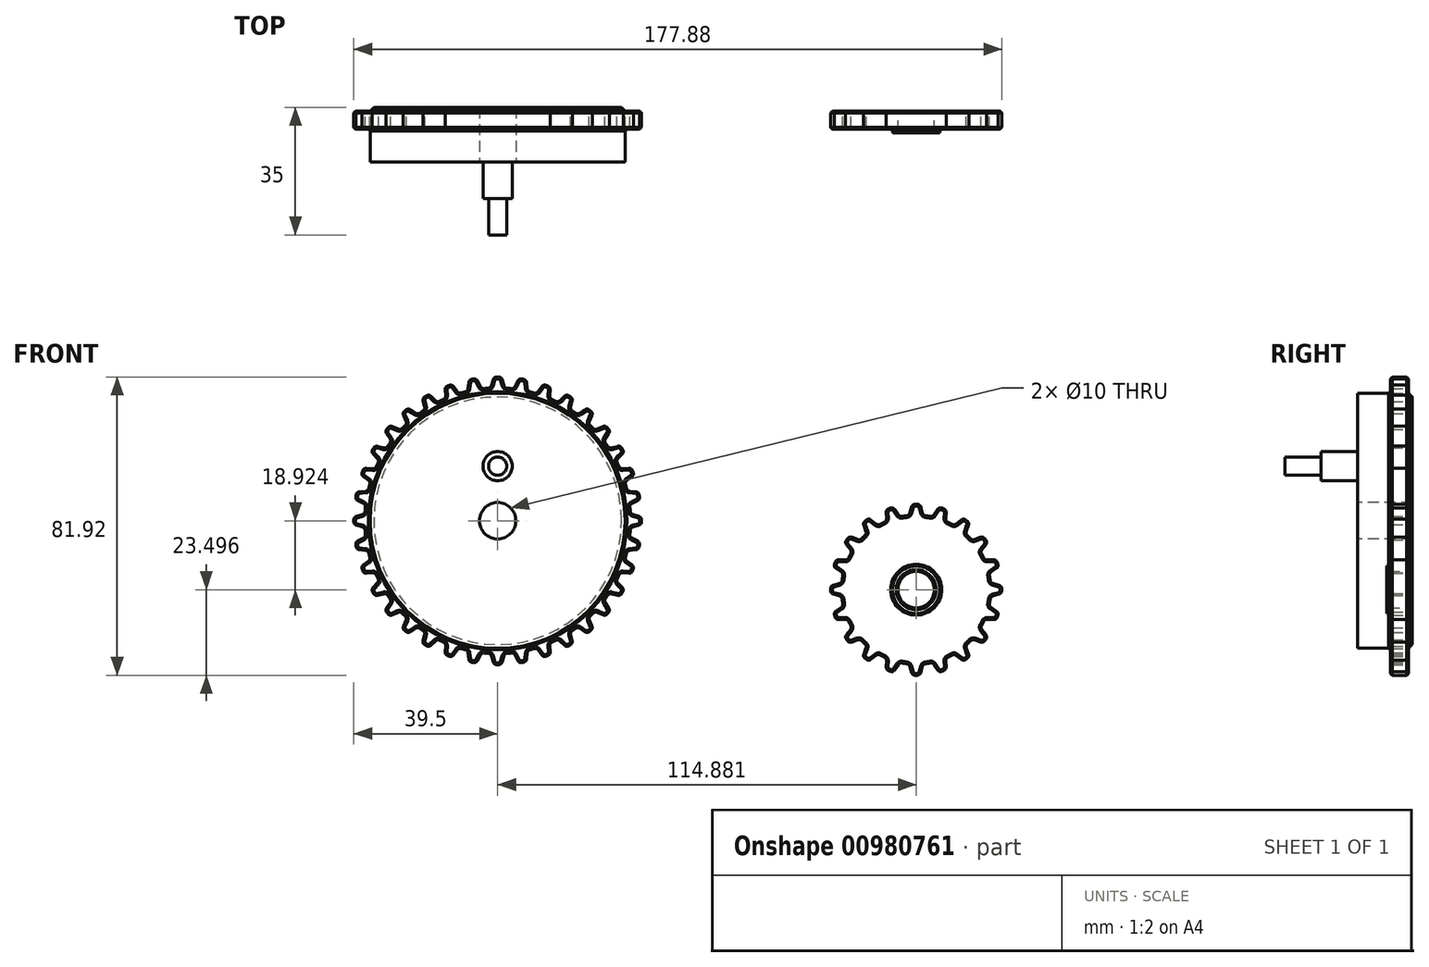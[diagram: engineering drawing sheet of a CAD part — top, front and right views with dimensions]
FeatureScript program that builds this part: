
annotation { "Feature Type Name" : "Feature", "Feature Type Description" : "" }
export const myFeature = defineFeature(function(context is Context, id is Id, definition is map)
    precondition{}
    {
        {
            var Q0;
            Q0=qCreatedBy(makeId("Front.planeOp"),FACE);
            var sketch = newSketch(context, id + "F0", { "sketchPlane" : qUnion([Q0])});
            skArc(sketch, "E0", {"start": v(1.03, 39.49) * mm, "mid": v(0, 39.5) * mm, "end": v(-1.03, 39.49) * mm});
            skCircle(sketch, "E1", {"center": v(0, 0) * mm, "radius": 36.5 * mm});
            skLineSegment(sketch, "E2", {"start": v(0, 0) * mm, "end": v(0, 36.5) * mm});
            skLineSegment(sketch, "E3", {"start": v(-1.03, 39.49) * mm, "end": v(-1.91, 36.45) * mm});
            skLineSegment(sketch, "E4", {"start": v(1.03, 39.49) * mm, "end": v(1.91, 36.45) * mm});
            skSolve(sketch);
        }
        {
            var Q0;
            {var subQ0=sQuery(id+"F0.wireOp",EDGE,"E1");var subQ1=makeQuery(id+"F0.imprint","IMPRINT",VERTEX,{"derivedFrom":subQ0});Q0=makeQuery(id+"F0.imprint","IMPRINT",FACE,{"disambiguationData":[TD([[makeQuery(id+"F0.imprint","IMPRINT",EDGE,{"disambiguationData":[TD([[subQ1,1.0]])],"derivedFrom":subQ0}),1.0]])]});}
            var Q1;
            Q1=makeQuery(id+"F0.imprint","IMPRINT",FACE,{"disambiguationData":[TD([[makeQuery(id+"F0.imprint","IMPRINT",EDGE,{"derivedFrom":sQuery(id+"F0.wireOp",EDGE,"E0")}),1.0]])]});
            extrude(context, id + "F1", {"entities" : qUnion([Q0, Q1]), "depth" : 5 * mm, "offsetDistance" : 25 * mm, "symmetric" : true});
        }
        {
            var Q0;
            Q0=makeQuery(id+"F1.opExtrude","SWEPT_EDGE",EDGE,{"disambiguationData":[OSD([sQuery(id+"F0.wireOp",EDGE,"E0"),sQuery(id+"F0.wireOp",EDGE,"E3")])]});
            var Q1;
            Q1=makeQuery(id+"F1.opExtrude","SWEPT_EDGE",EDGE,{"disambiguationData":[OSD([sQuery(id+"F0.wireOp",EDGE,"E0"),sQuery(id+"F0.wireOp",EDGE,"E4")])]});
            var Q2;
            Q2=makeQuery(id+"F1.opExtrude","SWEPT_EDGE",EDGE,{"disambiguationData":[OSD([sQuery(id+"F0.wireOp",EDGE,"E1"),sQuery(id+"F0.wireOp",EDGE,"E3")])]});
            var Q3;
            Q3=makeQuery(id+"F1.opExtrude","SWEPT_EDGE",EDGE,{"disambiguationData":[OSD([sQuery(id+"F0.wireOp",EDGE,"E1"),sQuery(id+"F0.wireOp",EDGE,"E4")])]});
            fillet(context, id + "F2", {"entities" : qUnion([Q0, Q1, Q2, Q3]), "radius" : 1 * mm, "tangentPropagation" : true, "allowEdgeOverflow" : false});
        }
        {
            var Q0;
            Q0=makeQuery(id+"F1.opExtrude","SWEPT_BODY",BODY,{"disambiguationData":[OSD([sQuery(id+"F0.wireOp",EDGE,"E0"),sQuery(id+"F0.wireOp",EDGE,"E1"),sQuery(id+"F0.wireOp",EDGE,"E3"),sQuery(id+"F0.wireOp",EDGE,"E4")])]});
            var Q1;
            Q1=makeQuery(id+"F1.opExtrude","SWEPT_FACE",FACE,{"disambiguationData":[OSD([sQuery(id+"F0.wireOp",EDGE,"E1")])]});
            circularPattern(context, id + "F3", {"operationType" : NewBodyOperationType.ADD, "entities" : qUnion([Q0]), "axis" : qUnion([Q1]), "angle" : 360 * degree, "instanceCount" : 36, "equalSpace" : true});
        }
        {
            var Q0;
            {var subQ0=makeQuery(id+"F1.opExtrude","CAP_FACE",FACE,{"disambiguationData":[OSD([sQuery(id+"F0.wireOp",EDGE,"E0"),sQuery(id+"F0.wireOp",EDGE,"E1"),sQuery(id+"F0.wireOp",EDGE,"E3"),sQuery(id+"F0.wireOp",EDGE,"E4")])],"isStart":false});Q0=makeQuery(id+"F3.boolean.opBoolean","MERGE",FACE,{"derivedFrom":[subQ0,makeQuery(id+"F3.opPattern","COPY",FACE,{"derivedFrom":subQ0,"instanceName":"1"}),makeQuery(id+"F3.opPattern","COPY",FACE,{"derivedFrom":subQ0,"instanceName":"2"}),makeQuery(id+"F3.opPattern","COPY",FACE,{"derivedFrom":subQ0,"instanceName":"3"}),makeQuery(id+"F3.opPattern","COPY",FACE,{"derivedFrom":subQ0,"instanceName":"4"}),makeQuery(id+"F3.opPattern","COPY",FACE,{"derivedFrom":subQ0,"instanceName":"5"}),makeQuery(id+"F3.opPattern","COPY",FACE,{"derivedFrom":subQ0,"instanceName":"6"}),makeQuery(id+"F3.opPattern","COPY",FACE,{"derivedFrom":subQ0,"instanceName":"7"}),makeQuery(id+"F3.opPattern","COPY",FACE,{"derivedFrom":subQ0,"instanceName":"8"}),makeQuery(id+"F3.opPattern","COPY",FACE,{"derivedFrom":subQ0,"instanceName":"9"}),makeQuery(id+"F3.opPattern","COPY",FACE,{"derivedFrom":subQ0,"instanceName":"10"}),makeQuery(id+"F3.opPattern","COPY",FACE,{"derivedFrom":subQ0,"instanceName":"11"}),makeQuery(id+"F3.opPattern","COPY",FACE,{"derivedFrom":subQ0,"instanceName":"12"}),makeQuery(id+"F3.opPattern","COPY",FACE,{"derivedFrom":subQ0,"instanceName":"13"}),makeQuery(id+"F3.opPattern","COPY",FACE,{"derivedFrom":subQ0,"instanceName":"14"}),makeQuery(id+"F3.opPattern","COPY",FACE,{"derivedFrom":subQ0,"instanceName":"15"}),makeQuery(id+"F3.opPattern","COPY",FACE,{"derivedFrom":subQ0,"instanceName":"16"}),makeQuery(id+"F3.opPattern","COPY",FACE,{"derivedFrom":subQ0,"instanceName":"17"}),makeQuery(id+"F3.opPattern","COPY",FACE,{"derivedFrom":subQ0,"instanceName":"18"}),makeQuery(id+"F3.opPattern","COPY",FACE,{"derivedFrom":subQ0,"instanceName":"19"}),makeQuery(id+"F3.opPattern","COPY",FACE,{"derivedFrom":subQ0,"instanceName":"20"}),makeQuery(id+"F3.opPattern","COPY",FACE,{"derivedFrom":subQ0,"instanceName":"21"}),makeQuery(id+"F3.opPattern","COPY",FACE,{"derivedFrom":subQ0,"instanceName":"22"}),makeQuery(id+"F3.opPattern","COPY",FACE,{"derivedFrom":subQ0,"instanceName":"23"}),makeQuery(id+"F3.opPattern","COPY",FACE,{"derivedFrom":subQ0,"instanceName":"24"}),makeQuery(id+"F3.opPattern","COPY",FACE,{"derivedFrom":subQ0,"instanceName":"25"}),makeQuery(id+"F3.opPattern","COPY",FACE,{"derivedFrom":subQ0,"instanceName":"26"}),makeQuery(id+"F3.opPattern","COPY",FACE,{"derivedFrom":subQ0,"instanceName":"27"}),makeQuery(id+"F3.opPattern","COPY",FACE,{"derivedFrom":subQ0,"instanceName":"28"}),makeQuery(id+"F3.opPattern","COPY",FACE,{"derivedFrom":subQ0,"instanceName":"29"}),makeQuery(id+"F3.opPattern","COPY",FACE,{"derivedFrom":subQ0,"instanceName":"30"}),makeQuery(id+"F3.opPattern","COPY",FACE,{"derivedFrom":subQ0,"instanceName":"31"}),makeQuery(id+"F3.opPattern","COPY",FACE,{"derivedFrom":subQ0,"instanceName":"32"}),makeQuery(id+"F3.opPattern","COPY",FACE,{"derivedFrom":subQ0,"instanceName":"33"}),makeQuery(id+"F3.opPattern","COPY",FACE,{"derivedFrom":subQ0,"instanceName":"34"}),makeQuery(id+"F3.opPattern","COPY",FACE,{"derivedFrom":subQ0,"instanceName":"35"})]});}
            var sketch = newSketch(context, id + "F4", { "sketchPlane" : qUnion([Q0])});
            skCircle(sketch, "E5", {"center": v(0, 0) * mm, "radius": 35 * mm});
            skSolve(sketch);
        }
        {
            var Q0;
            Q0=makeQuery(id+"F4.imprint","IMPRINT",FACE,{"disambiguationData":[TD([[makeQuery(id+"F4.imprint","IMPRINT",EDGE,{"derivedFrom":sQuery(id+"F4.wireOp",EDGE,"E5")}),1.0]])]});
            extrude(context, id + "F5", {"entities" : qUnion([Q0]), "operationType" : NewBodyOperationType.ADD, "depth" : 9 * mm, "offsetDistance" : 25 * mm});
        }
        {
            var Q0;
            {var subQ0=makeQuery(id+"F1.opExtrude","CAP_FACE",FACE,{"disambiguationData":[OSD([sQuery(id+"F0.wireOp",EDGE,"E0"),sQuery(id+"F0.wireOp",EDGE,"E1"),sQuery(id+"F0.wireOp",EDGE,"E3"),sQuery(id+"F0.wireOp",EDGE,"E4")])],"isStart":true});Q0=makeQuery(id+"F3.boolean.opBoolean","MERGE",FACE,{"derivedFrom":[subQ0,makeQuery(id+"F3.opPattern","COPY",FACE,{"derivedFrom":subQ0,"instanceName":"1"}),makeQuery(id+"F3.opPattern","COPY",FACE,{"derivedFrom":subQ0,"instanceName":"2"}),makeQuery(id+"F3.opPattern","COPY",FACE,{"derivedFrom":subQ0,"instanceName":"3"}),makeQuery(id+"F3.opPattern","COPY",FACE,{"derivedFrom":subQ0,"instanceName":"4"}),makeQuery(id+"F3.opPattern","COPY",FACE,{"derivedFrom":subQ0,"instanceName":"5"}),makeQuery(id+"F3.opPattern","COPY",FACE,{"derivedFrom":subQ0,"instanceName":"6"}),makeQuery(id+"F3.opPattern","COPY",FACE,{"derivedFrom":subQ0,"instanceName":"7"}),makeQuery(id+"F3.opPattern","COPY",FACE,{"derivedFrom":subQ0,"instanceName":"8"}),makeQuery(id+"F3.opPattern","COPY",FACE,{"derivedFrom":subQ0,"instanceName":"9"}),makeQuery(id+"F3.opPattern","COPY",FACE,{"derivedFrom":subQ0,"instanceName":"10"}),makeQuery(id+"F3.opPattern","COPY",FACE,{"derivedFrom":subQ0,"instanceName":"11"}),makeQuery(id+"F3.opPattern","COPY",FACE,{"derivedFrom":subQ0,"instanceName":"12"}),makeQuery(id+"F3.opPattern","COPY",FACE,{"derivedFrom":subQ0,"instanceName":"13"}),makeQuery(id+"F3.opPattern","COPY",FACE,{"derivedFrom":subQ0,"instanceName":"14"}),makeQuery(id+"F3.opPattern","COPY",FACE,{"derivedFrom":subQ0,"instanceName":"15"}),makeQuery(id+"F3.opPattern","COPY",FACE,{"derivedFrom":subQ0,"instanceName":"16"}),makeQuery(id+"F3.opPattern","COPY",FACE,{"derivedFrom":subQ0,"instanceName":"17"}),makeQuery(id+"F3.opPattern","COPY",FACE,{"derivedFrom":subQ0,"instanceName":"18"}),makeQuery(id+"F3.opPattern","COPY",FACE,{"derivedFrom":subQ0,"instanceName":"19"}),makeQuery(id+"F3.opPattern","COPY",FACE,{"derivedFrom":subQ0,"instanceName":"20"}),makeQuery(id+"F3.opPattern","COPY",FACE,{"derivedFrom":subQ0,"instanceName":"21"}),makeQuery(id+"F3.opPattern","COPY",FACE,{"derivedFrom":subQ0,"instanceName":"22"}),makeQuery(id+"F3.opPattern","COPY",FACE,{"derivedFrom":subQ0,"instanceName":"23"}),makeQuery(id+"F3.opPattern","COPY",FACE,{"derivedFrom":subQ0,"instanceName":"24"}),makeQuery(id+"F3.opPattern","COPY",FACE,{"derivedFrom":subQ0,"instanceName":"25"}),makeQuery(id+"F3.opPattern","COPY",FACE,{"derivedFrom":subQ0,"instanceName":"26"}),makeQuery(id+"F3.opPattern","COPY",FACE,{"derivedFrom":subQ0,"instanceName":"27"}),makeQuery(id+"F3.opPattern","COPY",FACE,{"derivedFrom":subQ0,"instanceName":"28"}),makeQuery(id+"F3.opPattern","COPY",FACE,{"derivedFrom":subQ0,"instanceName":"29"}),makeQuery(id+"F3.opPattern","COPY",FACE,{"derivedFrom":subQ0,"instanceName":"30"}),makeQuery(id+"F3.opPattern","COPY",FACE,{"derivedFrom":subQ0,"instanceName":"31"}),makeQuery(id+"F3.opPattern","COPY",FACE,{"derivedFrom":subQ0,"instanceName":"32"}),makeQuery(id+"F3.opPattern","COPY",FACE,{"derivedFrom":subQ0,"instanceName":"33"}),makeQuery(id+"F3.opPattern","COPY",FACE,{"derivedFrom":subQ0,"instanceName":"34"}),makeQuery(id+"F3.opPattern","COPY",FACE,{"derivedFrom":subQ0,"instanceName":"35"})]});}
            var sketch = newSketch(context, id + "F6", { "sketchPlane" : qUnion([Q0])});
            skCircle(sketch, "E6", {"center": v(0, 0) * mm, "radius": 35 * mm});
            skSolve(sketch);
        }
        {
            var Q0;
            Q0 = qSketchRegion(id + "F6", true);
            extrude(context, id + "F7", {"entities" : qUnion([Q0]), "operationType" : NewBodyOperationType.ADD, "depth" : 1 * mm, "offsetDistance" : 25 * mm});
        }
        {
            var Q0;
            Q0=makeQuery(id+"F7.opExtrude","CAP_EDGE",EDGE,{"disambiguationData":[OSD([sQuery(id+"F6.wireOp",EDGE,"E6")])],"isStart":false});
            chamfer(context, id + "F8", {"entities" : qUnion([Q0]), "width" : 1 * mm, "tangentPropagation" : true});
        }
        {
            var Q0;
            {var subQ0=makeQuery(id+"F1.opExtrude","CAP_FACE",FACE,{"disambiguationData":[OSD([sQuery(id+"F0.wireOp",EDGE,"E0"),sQuery(id+"F0.wireOp",EDGE,"E1"),sQuery(id+"F0.wireOp",EDGE,"E3"),sQuery(id+"F0.wireOp",EDGE,"E4")])],"isStart":false});Q0=makeQuery(id+"F3.boolean.opBoolean","MERGE",FACE,{"derivedFrom":[subQ0,makeQuery(id+"F3.opPattern","COPY",FACE,{"derivedFrom":subQ0,"instanceName":"1"}),makeQuery(id+"F3.opPattern","COPY",FACE,{"derivedFrom":subQ0,"instanceName":"2"}),makeQuery(id+"F3.opPattern","COPY",FACE,{"derivedFrom":subQ0,"instanceName":"3"}),makeQuery(id+"F3.opPattern","COPY",FACE,{"derivedFrom":subQ0,"instanceName":"4"}),makeQuery(id+"F3.opPattern","COPY",FACE,{"derivedFrom":subQ0,"instanceName":"5"}),makeQuery(id+"F3.opPattern","COPY",FACE,{"derivedFrom":subQ0,"instanceName":"6"}),makeQuery(id+"F3.opPattern","COPY",FACE,{"derivedFrom":subQ0,"instanceName":"7"}),makeQuery(id+"F3.opPattern","COPY",FACE,{"derivedFrom":subQ0,"instanceName":"8"}),makeQuery(id+"F3.opPattern","COPY",FACE,{"derivedFrom":subQ0,"instanceName":"9"}),makeQuery(id+"F3.opPattern","COPY",FACE,{"derivedFrom":subQ0,"instanceName":"10"}),makeQuery(id+"F3.opPattern","COPY",FACE,{"derivedFrom":subQ0,"instanceName":"11"}),makeQuery(id+"F3.opPattern","COPY",FACE,{"derivedFrom":subQ0,"instanceName":"12"}),makeQuery(id+"F3.opPattern","COPY",FACE,{"derivedFrom":subQ0,"instanceName":"13"}),makeQuery(id+"F3.opPattern","COPY",FACE,{"derivedFrom":subQ0,"instanceName":"14"}),makeQuery(id+"F3.opPattern","COPY",FACE,{"derivedFrom":subQ0,"instanceName":"15"}),makeQuery(id+"F3.opPattern","COPY",FACE,{"derivedFrom":subQ0,"instanceName":"16"}),makeQuery(id+"F3.opPattern","COPY",FACE,{"derivedFrom":subQ0,"instanceName":"17"}),makeQuery(id+"F3.opPattern","COPY",FACE,{"derivedFrom":subQ0,"instanceName":"18"}),makeQuery(id+"F3.opPattern","COPY",FACE,{"derivedFrom":subQ0,"instanceName":"19"}),makeQuery(id+"F3.opPattern","COPY",FACE,{"derivedFrom":subQ0,"instanceName":"20"}),makeQuery(id+"F3.opPattern","COPY",FACE,{"derivedFrom":subQ0,"instanceName":"21"}),makeQuery(id+"F3.opPattern","COPY",FACE,{"derivedFrom":subQ0,"instanceName":"22"}),makeQuery(id+"F3.opPattern","COPY",FACE,{"derivedFrom":subQ0,"instanceName":"23"}),makeQuery(id+"F3.opPattern","COPY",FACE,{"derivedFrom":subQ0,"instanceName":"24"}),makeQuery(id+"F3.opPattern","COPY",FACE,{"derivedFrom":subQ0,"instanceName":"25"}),makeQuery(id+"F3.opPattern","COPY",FACE,{"derivedFrom":subQ0,"instanceName":"26"}),makeQuery(id+"F3.opPattern","COPY",FACE,{"derivedFrom":subQ0,"instanceName":"27"}),makeQuery(id+"F3.opPattern","COPY",FACE,{"derivedFrom":subQ0,"instanceName":"28"}),makeQuery(id+"F3.opPattern","COPY",FACE,{"derivedFrom":subQ0,"instanceName":"29"}),makeQuery(id+"F3.opPattern","COPY",FACE,{"derivedFrom":subQ0,"instanceName":"30"}),makeQuery(id+"F3.opPattern","COPY",FACE,{"derivedFrom":subQ0,"instanceName":"31"}),makeQuery(id+"F3.opPattern","COPY",FACE,{"derivedFrom":subQ0,"instanceName":"32"}),makeQuery(id+"F3.opPattern","COPY",FACE,{"derivedFrom":subQ0,"instanceName":"33"}),makeQuery(id+"F3.opPattern","COPY",FACE,{"derivedFrom":subQ0,"instanceName":"34"}),makeQuery(id+"F3.opPattern","COPY",FACE,{"derivedFrom":subQ0,"instanceName":"35"})]});}
            var Q1;
            {var subQ0=makeQuery(id+"F1.opExtrude","CAP_FACE",FACE,{"disambiguationData":[OSD([sQuery(id+"F0.wireOp",EDGE,"E0"),sQuery(id+"F0.wireOp",EDGE,"E1"),sQuery(id+"F0.wireOp",EDGE,"E3"),sQuery(id+"F0.wireOp",EDGE,"E4")])],"isStart":true});Q1=makeQuery(id+"F3.boolean.opBoolean","MERGE",FACE,{"derivedFrom":[subQ0,makeQuery(id+"F3.opPattern","COPY",FACE,{"derivedFrom":subQ0,"instanceName":"1"}),makeQuery(id+"F3.opPattern","COPY",FACE,{"derivedFrom":subQ0,"instanceName":"2"}),makeQuery(id+"F3.opPattern","COPY",FACE,{"derivedFrom":subQ0,"instanceName":"3"}),makeQuery(id+"F3.opPattern","COPY",FACE,{"derivedFrom":subQ0,"instanceName":"4"}),makeQuery(id+"F3.opPattern","COPY",FACE,{"derivedFrom":subQ0,"instanceName":"5"}),makeQuery(id+"F3.opPattern","COPY",FACE,{"derivedFrom":subQ0,"instanceName":"6"}),makeQuery(id+"F3.opPattern","COPY",FACE,{"derivedFrom":subQ0,"instanceName":"7"}),makeQuery(id+"F3.opPattern","COPY",FACE,{"derivedFrom":subQ0,"instanceName":"8"}),makeQuery(id+"F3.opPattern","COPY",FACE,{"derivedFrom":subQ0,"instanceName":"9"}),makeQuery(id+"F3.opPattern","COPY",FACE,{"derivedFrom":subQ0,"instanceName":"10"}),makeQuery(id+"F3.opPattern","COPY",FACE,{"derivedFrom":subQ0,"instanceName":"11"}),makeQuery(id+"F3.opPattern","COPY",FACE,{"derivedFrom":subQ0,"instanceName":"12"}),makeQuery(id+"F3.opPattern","COPY",FACE,{"derivedFrom":subQ0,"instanceName":"13"}),makeQuery(id+"F3.opPattern","COPY",FACE,{"derivedFrom":subQ0,"instanceName":"14"}),makeQuery(id+"F3.opPattern","COPY",FACE,{"derivedFrom":subQ0,"instanceName":"15"}),makeQuery(id+"F3.opPattern","COPY",FACE,{"derivedFrom":subQ0,"instanceName":"16"}),makeQuery(id+"F3.opPattern","COPY",FACE,{"derivedFrom":subQ0,"instanceName":"17"}),makeQuery(id+"F3.opPattern","COPY",FACE,{"derivedFrom":subQ0,"instanceName":"18"}),makeQuery(id+"F3.opPattern","COPY",FACE,{"derivedFrom":subQ0,"instanceName":"19"}),makeQuery(id+"F3.opPattern","COPY",FACE,{"derivedFrom":subQ0,"instanceName":"20"}),makeQuery(id+"F3.opPattern","COPY",FACE,{"derivedFrom":subQ0,"instanceName":"21"}),makeQuery(id+"F3.opPattern","COPY",FACE,{"derivedFrom":subQ0,"instanceName":"22"}),makeQuery(id+"F3.opPattern","COPY",FACE,{"derivedFrom":subQ0,"instanceName":"23"}),makeQuery(id+"F3.opPattern","COPY",FACE,{"derivedFrom":subQ0,"instanceName":"24"}),makeQuery(id+"F3.opPattern","COPY",FACE,{"derivedFrom":subQ0,"instanceName":"25"}),makeQuery(id+"F3.opPattern","COPY",FACE,{"derivedFrom":subQ0,"instanceName":"26"}),makeQuery(id+"F3.opPattern","COPY",FACE,{"derivedFrom":subQ0,"instanceName":"27"}),makeQuery(id+"F3.opPattern","COPY",FACE,{"derivedFrom":subQ0,"instanceName":"28"}),makeQuery(id+"F3.opPattern","COPY",FACE,{"derivedFrom":subQ0,"instanceName":"29"}),makeQuery(id+"F3.opPattern","COPY",FACE,{"derivedFrom":subQ0,"instanceName":"30"}),makeQuery(id+"F3.opPattern","COPY",FACE,{"derivedFrom":subQ0,"instanceName":"31"}),makeQuery(id+"F3.opPattern","COPY",FACE,{"derivedFrom":subQ0,"instanceName":"32"}),makeQuery(id+"F3.opPattern","COPY",FACE,{"derivedFrom":subQ0,"instanceName":"33"}),makeQuery(id+"F3.opPattern","COPY",FACE,{"derivedFrom":subQ0,"instanceName":"34"}),makeQuery(id+"F3.opPattern","COPY",FACE,{"derivedFrom":subQ0,"instanceName":"35"})]});}
            chamfer(context, id + "F9", {"entities" : qUnion([Q0, Q1]), "width" : .5 * mm, "tangentPropagation" : true});
        }
        {
            var Q0;
            Q0=makeQuery(id+"F5.opExtrude","CAP_FACE",FACE,{"disambiguationData":[OSD([sQuery(id+"F4.wireOp",EDGE,"E5")])],"isStart":false});
            var sketch = newSketch(context, id + "F10", { "sketchPlane" : qUnion([Q0])});
            skCircle(sketch, "E7", {"center": v(0, 0) * mm, "radius": 5 * mm});
            skSolve(sketch);
        }
        {
            var Q0;
            Q0 = qSketchRegion(id + "F10", true);
            extrude(context, id + "F11", {"entities" : qUnion([Q0]), "operationType" : NewBodyOperationType.REMOVE, "oppositeDirection" : true, "depth" : 25 * mm, "offsetDistance" : 25 * mm});
        }
        {
            var Q0;
            Q0=makeQuery(id+"F5.opExtrude","CAP_FACE",FACE,{"disambiguationData":[OSD([sQuery(id+"F4.wireOp",EDGE,"E5")])],"isStart":false});
            var sketch = newSketch(context, id + "F12", { "sketchPlane" : qUnion([Q0])});
            skLineSegment(sketch, "E8", {"start": v(0, 0) * mm, "end": v(0, 15) * mm});
            skCircle(sketch, "E9", {"center": v(0, 15) * mm, "radius": 4 * mm});
            skCircle(sketch, "E10", {"center": v(0, 15) * mm, "radius": 2.5 * mm});
            skSolve(sketch);
        }
        {
            var Q0;
            Q0=makeQuery(id+"F12.imprint","IMPRINT",FACE,{"disambiguationData":[TD([[makeQuery(id+"F12.imprint","IMPRINT",EDGE,{"derivedFrom":sQuery(id+"F12.wireOp",EDGE,"E10")}),1.0]])]});
            extrude(context, id + "F13", {"entities" : qUnion([Q0]), "operationType" : NewBodyOperationType.ADD, "depth" : 20 * mm, "offsetDistance" : 25 * mm});
        }
        {
            var Q0;
            Q0=makeQuery(id+"F12.imprint","IMPRINT",FACE,{"disambiguationData":[TD([[makeQuery(id+"F12.imprint","IMPRINT",EDGE,{"derivedFrom":sQuery(id+"F12.wireOp",EDGE,"E9")}),1.0]])]});
            extrude(context, id + "F14", {"entities" : qUnion([Q0]), "operationType" : NewBodyOperationType.ADD, "depth" : 10 * mm, "offsetDistance" : 25 * mm});
        }
        {
            var Q0;
            Q0=qCreatedBy(makeId("Front.planeOp"),FACE);
            var sketch = newSketch(context, id + "F15", { "sketchPlane" : qUnion([Q0])});
            skArc(sketch, "E11", {"start": v(115.92, 4.55) * mm, "mid": v(114.88, 4.58) * mm, "end": v(113.85, 4.55) * mm});
            skArc(sketch, "E12", {"start": v(112.97, 1.49) * mm, "mid": v(114.88, -39.42) * mm, "end": v(116.8, 1.49) * mm});
            skLineSegment(sketch, "E13", {"start": v(114.88, -18.92) * mm, "end": v(114.88, 1.58) * mm});
            skLineSegment(sketch, "E14", {"start": v(113.85, 4.55) * mm, "end": v(112.97, 1.49) * mm});
            skLineSegment(sketch, "E15", {"start": v(115.92, 4.55) * mm, "end": v(116.8, 1.49) * mm});
            skLineSegment(sketch, "E16", {"start": v(114.88, 1.58) * mm, "end": v(114.88, 4.58) * mm});
            skCircle(sketch, "E17", {"center": v(114.88, -18.92) * mm, "radius": 5 * mm});
            skSolve(sketch);
        }
        {
            var Q0;
            Q0=makeQuery(id+"F15.imprint","IMPRINT",FACE,{"disambiguationData":[TD([[makeQuery(id+"F15.imprint","IMPRINT",EDGE,{"derivedFrom":sQuery(id+"F15.wireOp",EDGE,"E12")}),1.0]])]});
            extrude(context, id + "F16", {"entities" : qUnion([Q0]), "depth" : 5 * mm, "offsetDistance" : 25 * mm, "symmetric" : true});
        }
        {
            var Q0;
            Q0=makeQuery(id+"F16.opExtrude","SWEPT_EDGE",EDGE,{"disambiguationData":[OSD([sQuery(id+"F15.wireOp",EDGE,"E12"),sQuery(id+"F15.wireOp",EDGE,"E15")])]});
            var Q1;
            Q1=makeQuery(id+"F16.opExtrude","SWEPT_EDGE",EDGE,{"disambiguationData":[OSD([sQuery(id+"F15.wireOp",EDGE,"E11"),sQuery(id+"F15.wireOp",EDGE,"E15")])]});
            var Q2;
            Q2=makeQuery(id+"F16.opExtrude","SWEPT_EDGE",EDGE,{"disambiguationData":[OSD([sQuery(id+"F15.wireOp",EDGE,"E11"),sQuery(id+"F15.wireOp",EDGE,"E14")])]});
            var Q3;
            Q3=makeQuery(id+"F16.opExtrude","SWEPT_EDGE",EDGE,{"disambiguationData":[OSD([sQuery(id+"F15.wireOp",EDGE,"E12"),sQuery(id+"F15.wireOp",EDGE,"E14")])]});
            fillet(context, id + "F17", {"entities" : qUnion([Q0, Q1, Q2, Q3]), "radius" : 1 * mm, "tangentPropagation" : true, "allowEdgeOverflow" : false});
        }
        {
            var Q0;
            Q0=makeQuery(id+"F16.opExtrude","SWEPT_BODY",BODY,{"disambiguationData":[OSD([sQuery(id+"F15.wireOp",EDGE,"E11"),sQuery(id+"F15.wireOp",EDGE,"E12"),sQuery(id+"F15.wireOp",EDGE,"E14"),sQuery(id+"F15.wireOp",EDGE,"E15")])]});
            var Q1;
            Q1=makeQuery(id+"F16.opExtrude","SWEPT_FACE",FACE,{"disambiguationData":[OSD([sQuery(id+"F15.wireOp",EDGE,"E12")])]});
            circularPattern(context, id + "F18", {"operationType" : NewBodyOperationType.ADD, "entities" : qUnion([Q0]), "axis" : qUnion([Q1]), "angle" : 360 * degree, "instanceCount" : 20, "equalSpace" : true});
        }
        {
            var Q0;
            {var subQ0=makeQuery(id+"F16.opExtrude","CAP_FACE",FACE,{"disambiguationData":[OSD([sQuery(id+"F15.wireOp",EDGE,"E11"),sQuery(id+"F15.wireOp",EDGE,"E12"),sQuery(id+"F15.wireOp",EDGE,"E14"),sQuery(id+"F15.wireOp",EDGE,"E15")])],"isStart":true});Q0=makeQuery(id+"F18.boolean.opBoolean","MERGE",FACE,{"derivedFrom":[subQ0,makeQuery(id+"F18.opPattern","COPY",FACE,{"derivedFrom":subQ0,"instanceName":"1"}),makeQuery(id+"F18.opPattern","COPY",FACE,{"derivedFrom":subQ0,"instanceName":"2"}),makeQuery(id+"F18.opPattern","COPY",FACE,{"derivedFrom":subQ0,"instanceName":"3"}),makeQuery(id+"F18.opPattern","COPY",FACE,{"derivedFrom":subQ0,"instanceName":"4"}),makeQuery(id+"F18.opPattern","COPY",FACE,{"derivedFrom":subQ0,"instanceName":"5"}),makeQuery(id+"F18.opPattern","COPY",FACE,{"derivedFrom":subQ0,"instanceName":"6"}),makeQuery(id+"F18.opPattern","COPY",FACE,{"derivedFrom":subQ0,"instanceName":"7"}),makeQuery(id+"F18.opPattern","COPY",FACE,{"derivedFrom":subQ0,"instanceName":"8"}),makeQuery(id+"F18.opPattern","COPY",FACE,{"derivedFrom":subQ0,"instanceName":"9"}),makeQuery(id+"F18.opPattern","COPY",FACE,{"derivedFrom":subQ0,"instanceName":"10"}),makeQuery(id+"F18.opPattern","COPY",FACE,{"derivedFrom":subQ0,"instanceName":"11"}),makeQuery(id+"F18.opPattern","COPY",FACE,{"derivedFrom":subQ0,"instanceName":"12"}),makeQuery(id+"F18.opPattern","COPY",FACE,{"derivedFrom":subQ0,"instanceName":"13"}),makeQuery(id+"F18.opPattern","COPY",FACE,{"derivedFrom":subQ0,"instanceName":"14"}),makeQuery(id+"F18.opPattern","COPY",FACE,{"derivedFrom":subQ0,"instanceName":"15"}),makeQuery(id+"F18.opPattern","COPY",FACE,{"derivedFrom":subQ0,"instanceName":"16"}),makeQuery(id+"F18.opPattern","COPY",FACE,{"derivedFrom":subQ0,"instanceName":"17"}),makeQuery(id+"F18.opPattern","COPY",FACE,{"derivedFrom":subQ0,"instanceName":"18"}),makeQuery(id+"F18.opPattern","COPY",FACE,{"derivedFrom":subQ0,"instanceName":"19"})]});}
            chamfer(context, id + "F19", {"entities" : qUnion([Q0]), "width" : .5 * mm, "tangentPropagation" : true});
        }
        {
            var Q0;
            {var subQ0=makeQuery(id+"F16.opExtrude","CAP_FACE",FACE,{"disambiguationData":[OSD([sQuery(id+"F15.wireOp",EDGE,"E11"),sQuery(id+"F15.wireOp",EDGE,"E12"),sQuery(id+"F15.wireOp",EDGE,"E14"),sQuery(id+"F15.wireOp",EDGE,"E15"),sQuery(id+"F15.wireOp",EDGE,"E17")])],"isStart":false});Q0=makeQuery(id+"F18.boolean.opBoolean","MERGE",FACE,{"derivedFrom":[subQ0,makeQuery(id+"F18.opPattern","COPY",FACE,{"derivedFrom":subQ0,"instanceName":"1"}),makeQuery(id+"F18.opPattern","COPY",FACE,{"derivedFrom":subQ0,"instanceName":"2"}),makeQuery(id+"F18.opPattern","COPY",FACE,{"derivedFrom":subQ0,"instanceName":"3"}),makeQuery(id+"F18.opPattern","COPY",FACE,{"derivedFrom":subQ0,"instanceName":"4"}),makeQuery(id+"F18.opPattern","COPY",FACE,{"derivedFrom":subQ0,"instanceName":"5"}),makeQuery(id+"F18.opPattern","COPY",FACE,{"derivedFrom":subQ0,"instanceName":"6"}),makeQuery(id+"F18.opPattern","COPY",FACE,{"derivedFrom":subQ0,"instanceName":"7"}),makeQuery(id+"F18.opPattern","COPY",FACE,{"derivedFrom":subQ0,"instanceName":"8"}),makeQuery(id+"F18.opPattern","COPY",FACE,{"derivedFrom":subQ0,"instanceName":"9"}),makeQuery(id+"F18.opPattern","COPY",FACE,{"derivedFrom":subQ0,"instanceName":"10"}),makeQuery(id+"F18.opPattern","COPY",FACE,{"derivedFrom":subQ0,"instanceName":"11"}),makeQuery(id+"F18.opPattern","COPY",FACE,{"derivedFrom":subQ0,"instanceName":"12"}),makeQuery(id+"F18.opPattern","COPY",FACE,{"derivedFrom":subQ0,"instanceName":"13"}),makeQuery(id+"F18.opPattern","COPY",FACE,{"derivedFrom":subQ0,"instanceName":"14"}),makeQuery(id+"F18.opPattern","COPY",FACE,{"derivedFrom":subQ0,"instanceName":"15"}),makeQuery(id+"F18.opPattern","COPY",FACE,{"derivedFrom":subQ0,"instanceName":"16"}),makeQuery(id+"F18.opPattern","COPY",FACE,{"derivedFrom":subQ0,"instanceName":"17"}),makeQuery(id+"F18.opPattern","COPY",FACE,{"derivedFrom":subQ0,"instanceName":"18"}),makeQuery(id+"F18.opPattern","COPY",FACE,{"derivedFrom":subQ0,"instanceName":"19"})]});}
            var sketch = newSketch(context, id + "F20", { "sketchPlane" : qUnion([Q0])});
            skCircle(sketch, "E18", {"center": v(114.88, -18.92) * mm, "radius": 6.5 * mm});
            skCircle(sketch, "E19", {"center": v(114.88, -18.92) * mm, "radius": 5 * mm});
            skSolve(sketch);
        }
        {
            var Q0;
            Q0 = qSketchRegion(id + "F20", true);
            extrude(context, id + "F21", {"entities" : qUnion([Q0]), "operationType" : NewBodyOperationType.ADD, "depth" : 1 * mm, "offsetDistance" : 25 * mm});
        }
        {
            var Q0;
            {var subQ0=makeQuery(id+"F16.opExtrude","CAP_FACE",FACE,{"disambiguationData":[OSD([sQuery(id+"F15.wireOp",EDGE,"E11"),sQuery(id+"F15.wireOp",EDGE,"E12"),sQuery(id+"F15.wireOp",EDGE,"E14"),sQuery(id+"F15.wireOp",EDGE,"E15"),sQuery(id+"F15.wireOp",EDGE,"E17")])],"isStart":false});Q0=makeQuery(id+"F18.boolean.opBoolean","MERGE",FACE,{"derivedFrom":[subQ0,makeQuery(id+"F18.opPattern","COPY",FACE,{"derivedFrom":subQ0,"instanceName":"1"}),makeQuery(id+"F18.opPattern","COPY",FACE,{"derivedFrom":subQ0,"instanceName":"2"}),makeQuery(id+"F18.opPattern","COPY",FACE,{"derivedFrom":subQ0,"instanceName":"3"}),makeQuery(id+"F18.opPattern","COPY",FACE,{"derivedFrom":subQ0,"instanceName":"4"}),makeQuery(id+"F18.opPattern","COPY",FACE,{"derivedFrom":subQ0,"instanceName":"5"}),makeQuery(id+"F18.opPattern","COPY",FACE,{"derivedFrom":subQ0,"instanceName":"6"}),makeQuery(id+"F18.opPattern","COPY",FACE,{"derivedFrom":subQ0,"instanceName":"7"}),makeQuery(id+"F18.opPattern","COPY",FACE,{"derivedFrom":subQ0,"instanceName":"8"}),makeQuery(id+"F18.opPattern","COPY",FACE,{"derivedFrom":subQ0,"instanceName":"9"}),makeQuery(id+"F18.opPattern","COPY",FACE,{"derivedFrom":subQ0,"instanceName":"10"}),makeQuery(id+"F18.opPattern","COPY",FACE,{"derivedFrom":subQ0,"instanceName":"11"}),makeQuery(id+"F18.opPattern","COPY",FACE,{"derivedFrom":subQ0,"instanceName":"12"}),makeQuery(id+"F18.opPattern","COPY",FACE,{"derivedFrom":subQ0,"instanceName":"13"}),makeQuery(id+"F18.opPattern","COPY",FACE,{"derivedFrom":subQ0,"instanceName":"14"}),makeQuery(id+"F18.opPattern","COPY",FACE,{"derivedFrom":subQ0,"instanceName":"15"}),makeQuery(id+"F18.opPattern","COPY",FACE,{"derivedFrom":subQ0,"instanceName":"16"}),makeQuery(id+"F18.opPattern","COPY",FACE,{"derivedFrom":subQ0,"instanceName":"17"}),makeQuery(id+"F18.opPattern","COPY",FACE,{"derivedFrom":subQ0,"instanceName":"18"}),makeQuery(id+"F18.opPattern","COPY",FACE,{"derivedFrom":subQ0,"instanceName":"19"})]});}
            var Q1;
            Q1=makeQuery(id+"F21.opExtrude","CAP_EDGE",EDGE,{"disambiguationData":[OSD([sQuery(id+"F20.wireOp",EDGE,"E19")])],"isStart":false});
            chamfer(context, id + "F22", {"entities" : qUnion([Q0, Q1]), "width" : .5 * mm, "tangentPropagation" : true});
        }
    });
